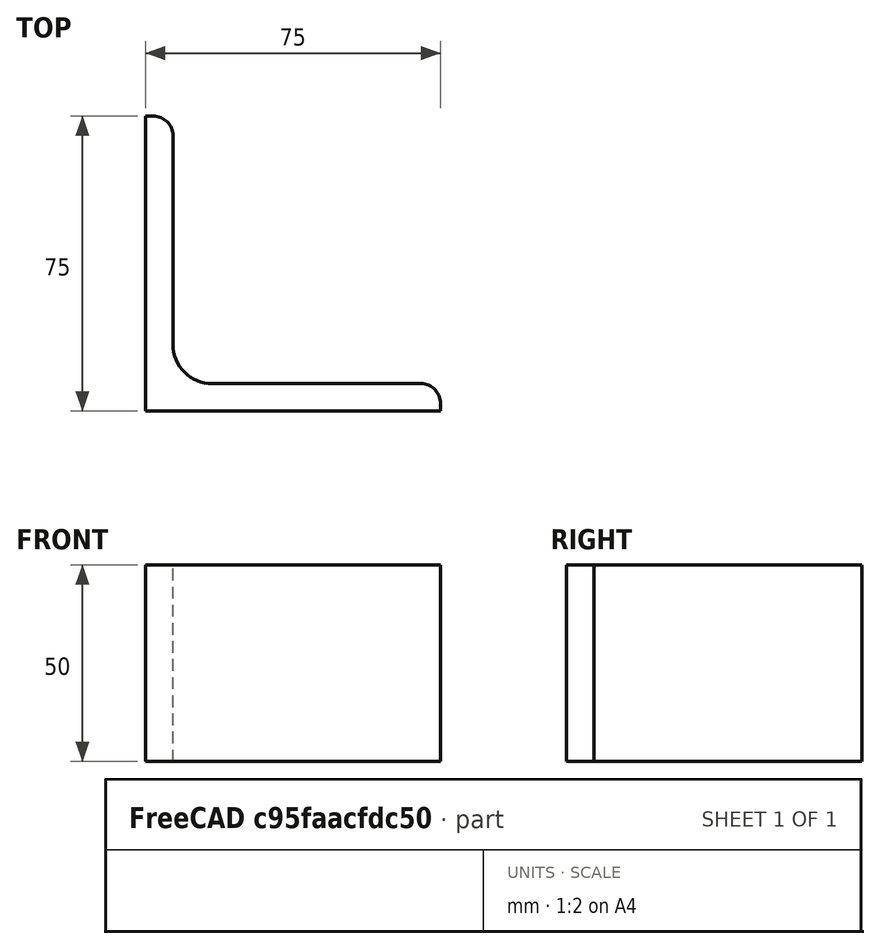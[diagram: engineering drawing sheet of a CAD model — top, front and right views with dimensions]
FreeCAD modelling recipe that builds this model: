
FCSTD DOCUMENT  (FreeCAD 0.15R4671 (Git))
Label: Angle Bar L75x75x7 EN10056 S235JR
License: All rights reserved
LicenseURL: http://en.wikipedia.org/wiki/All_rights_reserved
objects: Sketcher::SketchObject×1, Part::Extrusion×1
note: 2 computed .brp shape members not serialized (recipe doc carries the construction recipe); baked Part::Feature solids carry a one-line shape summary decoded from their .brp

FEATURE [Sketcher::SketchObject] Sketch
  sketch-geometry (9):
    g0: LineSegment StartX=0 StartY=0 StartZ=0 EndX=75 EndY=0 EndZ=0
    g1: LineSegment StartX=75 StartY=0 StartZ=0 EndX=75 EndY=2 EndZ=0
    g2: LineSegment StartX=70 StartY=7 StartZ=0 EndX=17 EndY=7 EndZ=0
    g3: LineSegment StartX=0 StartY=0 StartZ=0 EndX=0 EndY=75 EndZ=0
    g4: LineSegment StartX=0 StartY=75 StartZ=0 EndX=2 EndY=75 EndZ=0
    g5: LineSegment StartX=7 StartY=70 StartZ=0 EndX=7 EndY=17 EndZ=0
    g6: ArcOfCircle CenterX=17 CenterY=17 CenterZ=0 NormalX=0 NormalY=0 NormalZ=1 Radius=10 StartAngle=3.14159 EndAngle=4.71239
    g7: ArcOfCircle CenterX=2 CenterY=70 CenterZ=0 NormalX=0 NormalY=0 NormalZ=1 Radius=5 StartAngle=0 EndAngle=1.5708
    g8: ArcOfCircle CenterX=70 CenterY=2 CenterZ=0 NormalX=0 NormalY=0 NormalZ=1 Radius=5 StartAngle=0 EndAngle=1.5708
  constraints (23):
    c: Coincident(g0,g-1)
    c: Horizontal(g0)
    c: Coincident(g1,g0)
    c: Vertical(g1)
    c: Horizontal(g2)
    c: Coincident(g3,g-1)
    c: Vertical(g3)
    c: Coincident(g4,g3)
    c: Horizontal(g4)
    c: Vertical(g5)
    c: Tangent(g5,g6) = -1.5708
    c: Tangent(g2,g6) = 1.5708
    c: Tangent(g4,g7) = 1.5708
    c: Tangent(g5,g7) = 1.5708
    c: Tangent(g2,g8) = -1.5708
    c: Tangent(g1,g8) = -1.5708
    c: DistanceX(g0) = 75
    c: DistanceY(g3) = 75
    c: DistanceY(g0,g2) = 7
    c: DistanceX(g3,g5) = 7
    c: Radius(g6) = 10
    c: Radius(g8) = 5
    c: Radius(g7) = 5
FEATURE [Part::Extrusion] Extrude  label="Angle Bar L75x75x7 EN10056 S235JR"
  Base = -> Sketch
  Dir = (0,0,50)
  Solid = true
